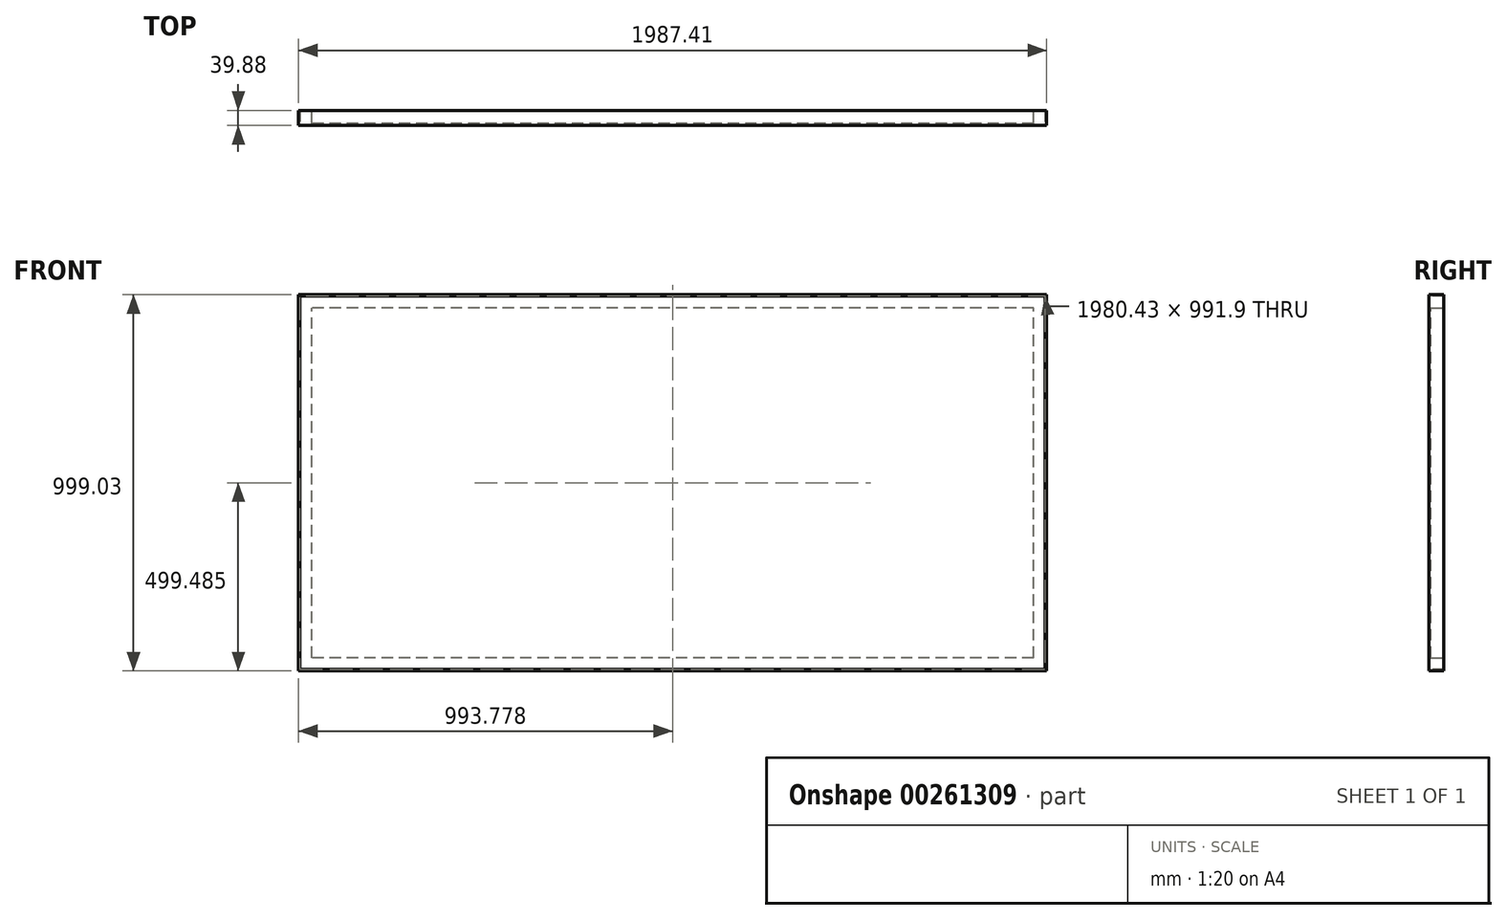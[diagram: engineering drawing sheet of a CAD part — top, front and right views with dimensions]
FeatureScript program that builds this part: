
annotation { "Feature Type Name" : "Feature", "Feature Type Description" : "" }
export const myFeature = defineFeature(function(context is Context, id is Id, definition is map)
    precondition{}
    {
        {
            var Q0;
            Q0=qCreatedBy(makeId("Top.planeOp"),FACE);
            var sketch = newSketch(context, id + "F0", { "sketchPlane" : qUnion([Q0])});
            skLineSegment(sketch, "E0.bottom", {"start": v(0, 0) * mm, "end": v(1987.55, 0) * mm});
            skLineSegment(sketch, "E0.top", {"start": v(0, 39.88) * mm, "end": v(1987.55, 39.88) * mm});
            skLineSegment(sketch, "E0.left", {"start": v(0, 0) * mm, "end": v(0, 39.88) * mm});
            skLineSegment(sketch, "E0.right", {"start": v(1987.55, 0) * mm, "end": v(1987.55, 39.88) * mm});
            skSolve(sketch);
        }
        {
            var Q0;
            Q0 = qSketchRegion(id + "F0", true);
            extrude(context, id + "F1", {"entities" : qUnion([Q0]), "depth" : 998.98 * mm});
        }
        {
            var Q0;
            Q0=makeQuery(id+"F1.opExtrude","SWEPT_FACE",FACE,{"disambiguationData":[OSD([sQuery(id+"F0.wireOp",EDGE,"E0.top")])]});
            var sketch = newSketch(context, id + "F2", { "sketchPlane" : qUnion([Q0])});
            skLineSegment(sketch, "E1.bottom", {"start": v(-1952.5, 35.05) * mm, "end": v(-35.05, 35.05) * mm});
            skLineSegment(sketch, "E1.top", {"start": v(-1952.5, 963.93) * mm, "end": v(-35.05, 963.93) * mm});
            skLineSegment(sketch, "E1.left", {"start": v(-1952.5, 35.05) * mm, "end": v(-1952.5, 963.93) * mm});
            skLineSegment(sketch, "E1.right", {"start": v(-35.05, 35.05) * mm, "end": v(-35.05, 963.93) * mm});
            skSolve(sketch);
        }
        {
            var Q0;
            Q0 = qSketchRegion(id + "F2", true);
            extrude(context, id + "F3", {"entities" : qUnion([Q0]), "operationType" : NewBodyOperationType.REMOVE, "oppositeDirection" : true, "depth" : 35.05 * mm});
        }
        {
            var Q0;
            Q0=makeQuery(id+"F1.opExtrude","SWEPT_FACE",FACE,{"disambiguationData":[OSD([sQuery(id+"F0.wireOp",EDGE,"E0.bottom")])]});
            var sketch = newSketch(context, id + "F4", { "sketchPlane" : qUnion([Q0])});
            skLineSegment(sketch, "E2.bottom", {"start": v(3.56, 3.56) * mm, "end": v(1984, 3.56) * mm});
            skLineSegment(sketch, "E2.top", {"start": v(3.56, 995.43) * mm, "end": v(1984, 995.43) * mm});
            skLineSegment(sketch, "E2.left", {"start": v(3.56, 3.56) * mm, "end": v(3.56, 995.43) * mm});
            skLineSegment(sketch, "E2.right", {"start": v(1984, 3.56) * mm, "end": v(1984, 995.43) * mm});
            skLineSegment(sketch, "E3.bottom", {"start": v(0, 0) * mm, "end": v(1987.55, 0) * mm});
            skLineSegment(sketch, "E3.top", {"start": v(0, 998.98) * mm, "end": v(1987.55, 998.98) * mm});
            skLineSegment(sketch, "E3.left", {"start": v(0, 0) * mm, "end": v(0, 998.98) * mm});
            skLineSegment(sketch, "E3.right", {"start": v(1987.55, 0) * mm, "end": v(1987.55, 998.98) * mm});
            skSolve(sketch);
        }
        {
            var Q0;
            Q0 = qSketchRegion(id + "F4", true);
            extrude(context, id + "F5", {"entities" : qUnion([Q0]), "operationType" : NewBodyOperationType.REMOVE, "oppositeDirection" : true, "depth" : 39.88 * mm});
        }
        {
            var Q0;
            Q0=makeQuery(id+"F4.imprint","IMPRINT",FACE,{"disambiguationData":[TD([[makeQuery(id+"F4.imprint","IMPRINT",EDGE,{"derivedFrom":sQuery(id+"F4.wireOp",EDGE,"E2.bottom")}),1.0]])]});
            var sketch = newSketch(context, id + "F6", { "sketchPlane" : qUnion([Q0])});
            skLineSegment(sketch, "E4.bottom", {"start": v(0, 0) * mm, "end": v(1987.4, 0) * mm});
            skLineSegment(sketch, "E4.top", {"start": v(0, 999.03) * mm, "end": v(1987.4, 999.03) * mm});
            skLineSegment(sketch, "E4.left", {"start": v(0, 0) * mm, "end": v(0, 999.03) * mm});
            skLineSegment(sketch, "E4.right", {"start": v(1987.4, 0) * mm, "end": v(1987.4, 999.03) * mm});
            skLineSegment(sketch, "E5.bottom", {"start": v(3.56, 3.53) * mm, "end": v(1984, 3.53) * mm});
            skLineSegment(sketch, "E5.top", {"start": v(3.56, 995.44) * mm, "end": v(1984, 995.44) * mm});
            skLineSegment(sketch, "E5.left", {"start": v(3.56, 3.53) * mm, "end": v(3.56, 995.44) * mm});
            skLineSegment(sketch, "E5.right", {"start": v(1984, 3.53) * mm, "end": v(1984, 995.44) * mm});
            skSolve(sketch);
        }
        {
            var Q0;
            Q0 = qSketchRegion(id + "F6", true);
            extrude(context, id + "F7", {"entities" : qUnion([Q0]), "oppositeDirection" : true, "depth" : 39.88 * mm});
        }
    });
